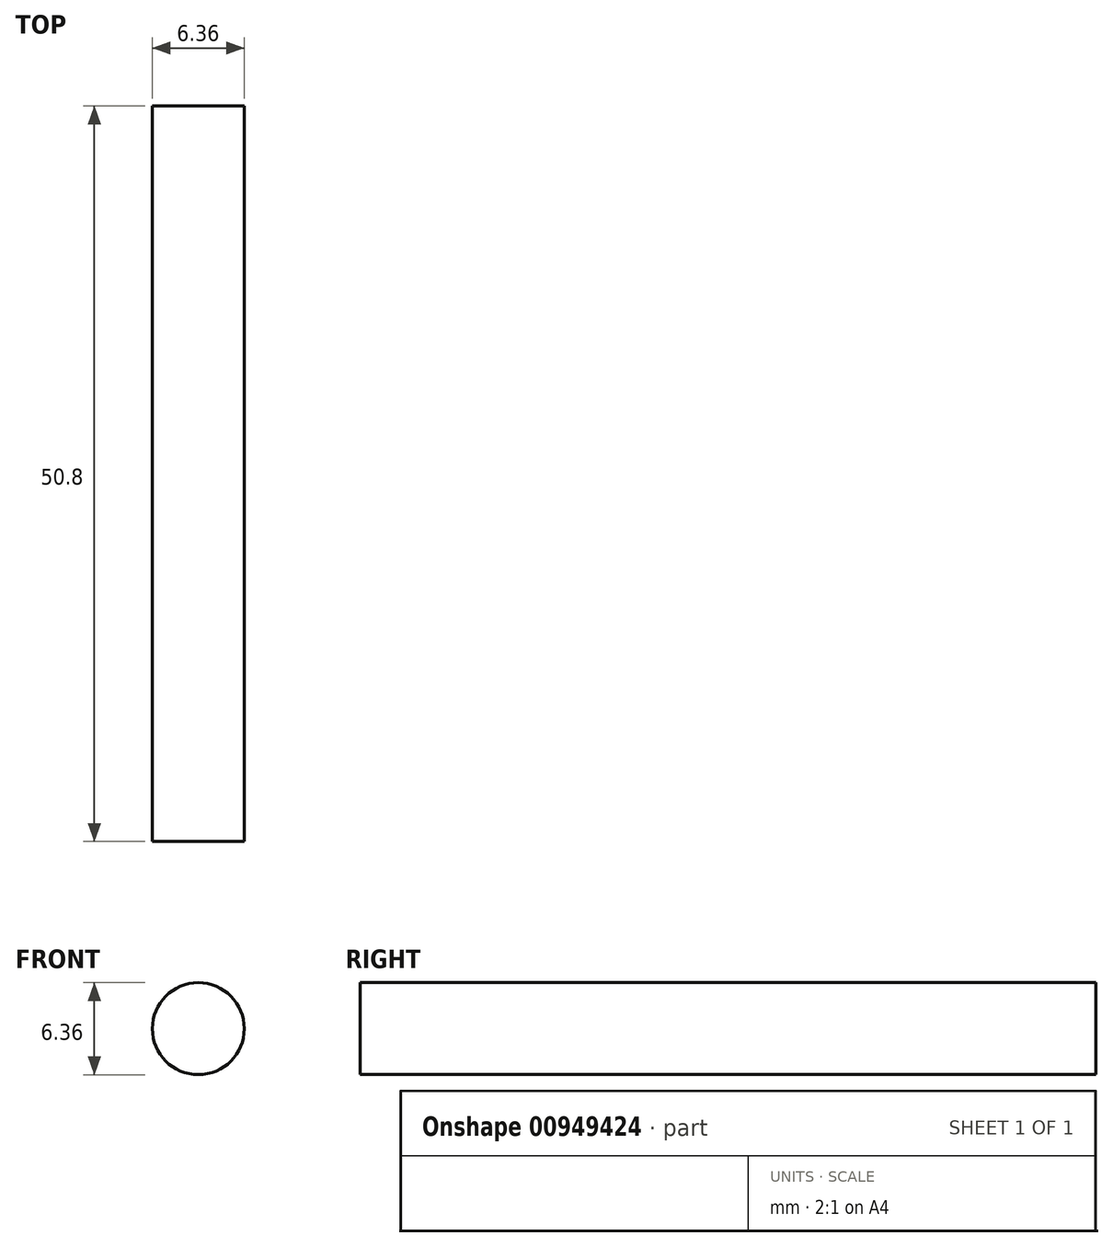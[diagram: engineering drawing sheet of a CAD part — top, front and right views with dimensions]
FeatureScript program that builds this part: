
annotation { "Feature Type Name" : "Feature", "Feature Type Description" : "" }
export const myFeature = defineFeature(function(context is Context, id is Id, definition is map)
    precondition{}
    {
        {
            var Q0;
            Q0=qCreatedBy(makeId("Front.planeOp"),FACE);
            var sketch = newSketch(context, id + "F0", { "sketchPlane" : qUnion([Q0])});
            skCircle(sketch, "E0", {"center": v(0, 0) * mm, "radius": 3.18 * mm});
            skSolve(sketch);
        }
        {
            var Q0;
            Q0=makeQuery(id+"F0.imprint","IMPRINT",FACE,{"disambiguationData":[TD([[makeQuery(id+"F0.imprint","IMPRINT",EDGE,{"derivedFrom":sQuery(id+"F0.wireOp",EDGE,"E0")}),1.0]])]});
            extrude(context, id + "F1", {"entities" : qUnion([Q0]), "endBound" : BoundingType.SYMMETRIC, "depth" : 50.8 * mm, "offsetDistance" : 25.4 * mm});
        }
    });
